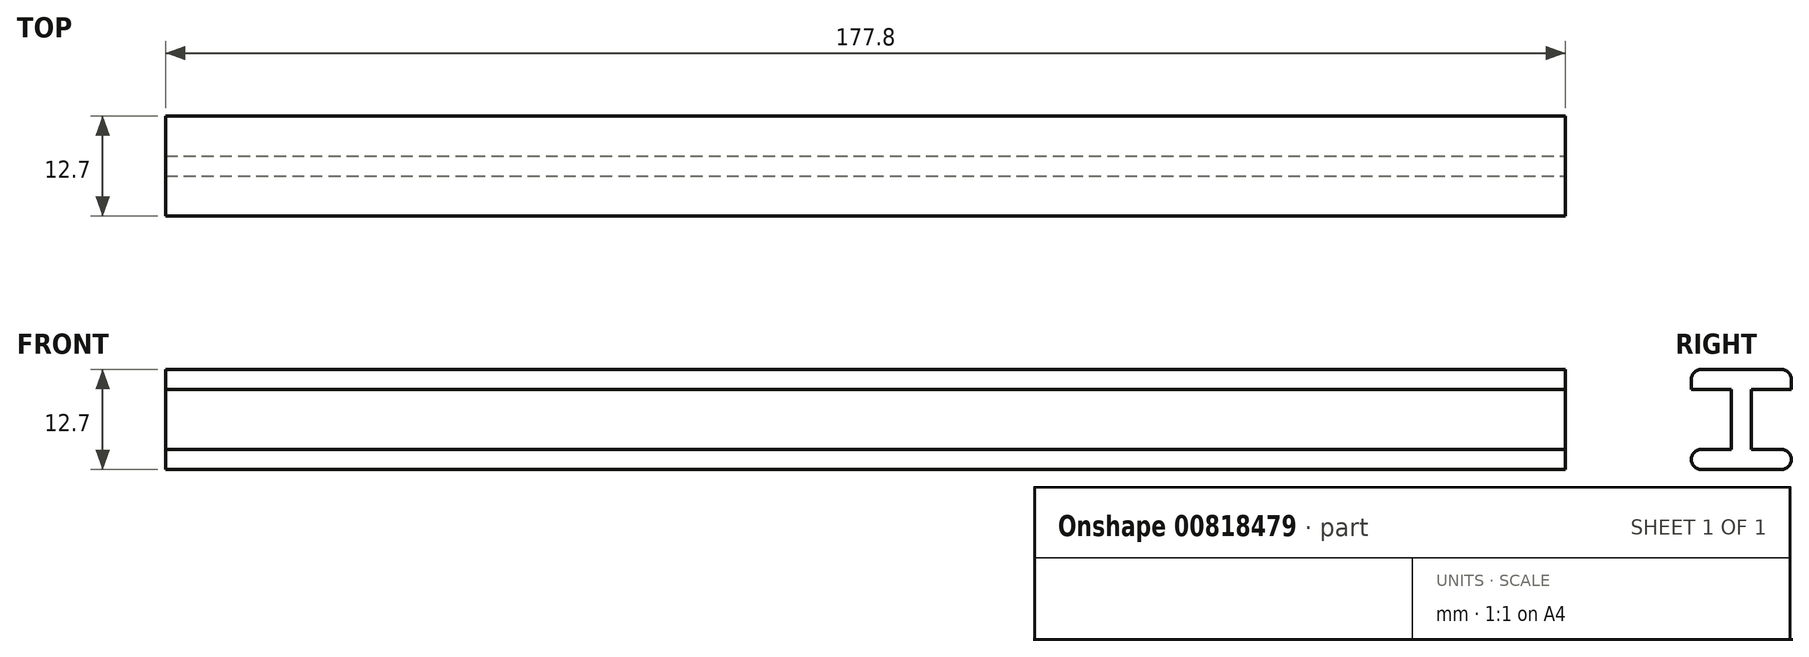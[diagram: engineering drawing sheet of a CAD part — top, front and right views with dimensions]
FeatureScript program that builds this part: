
annotation { "Feature Type Name" : "Feature", "Feature Type Description" : "" }
export const myFeature = defineFeature(function(context is Context, id is Id, definition is map)
    precondition{}
    {
        {
            var Q0;
            Q0=qCreatedBy(makeId("Top.planeOp"),FACE);
            var sketch = newSketch(context, id + "F0", { "sketchPlane" : qUnion([Q0])});
            skLineSegment(sketch, "E0.bottom", {"start": v(-88.9, 6.35) * mm, "end": v(88.9, 6.35) * mm});
            skLineSegment(sketch, "E0.top", {"start": v(-88.9, -6.35) * mm, "end": v(88.9, -6.35) * mm});
            skLineSegment(sketch, "E0.left", {"start": v(-88.9, 6.35) * mm, "end": v(-88.9, -6.35) * mm});
            skLineSegment(sketch, "E0.right", {"start": v(88.9, 6.35) * mm, "end": v(88.9, -6.35) * mm});
            skPoint(sketch, "E0.middle", {"position": v(0, 0) * mm});
            skSolve(sketch);
        }
        {
            var Q0;
            Q0=makeQuery(id+"F0.imprint","IMPRINT",FACE,{"disambiguationData":[TD([[makeQuery(id+"F0.imprint","IMPRINT",EDGE,{"derivedFrom":sQuery(id+"F0.wireOp",EDGE,"E0.bottom")}),-1.0]])]});
            extrude(context, id + "F1", {"entities" : qUnion([Q0]), "depth" : 12.7 * mm, "offsetDistance" : 25.4 * mm});
        }
        {
            var Q0;
            Q0=makeQuery(id+"F1.opExtrude","CAP_EDGE",EDGE,{"disambiguationData":[OSD([sQuery(id+"F0.wireOp",EDGE,"E0.bottom")])],"isStart":true});
            var Q1;
            Q1=makeQuery(id+"F1.opExtrude","CAP_EDGE",EDGE,{"disambiguationData":[OSD([sQuery(id+"F0.wireOp",EDGE,"E0.top")])],"isStart":false});
            var Q2;
            Q2=makeQuery(id+"F1.opExtrude","CAP_EDGE",EDGE,{"disambiguationData":[OSD([sQuery(id+"F0.wireOp",EDGE,"E0.top")])],"isStart":true});
            var Q3;
            Q3=makeQuery(id+"F1.opExtrude","CAP_EDGE",EDGE,{"disambiguationData":[OSD([sQuery(id+"F0.wireOp",EDGE,"E0.bottom")])],"isStart":false});
            fillet(context, id + "F2", {"entities" : qUnion([Q0, Q1, Q2, Q3]), "radius" : 1.27 * mm, "tangentPropagation" : true, "allowEdgeOverflow" : false});
        }
        {
            var Q0;
            Q0=makeQuery(id+"F1.opExtrude","SWEPT_FACE",FACE,{"disambiguationData":[OSD([sQuery(id+"F0.wireOp",EDGE,"E0.right")])]});
            var sketch = newSketch(context, id + "F3", { "sketchPlane" : qUnion([Q0])});
            skLineSegment(sketch, "E1.bottom", {"start": v(-6.35, 10.16) * mm, "end": v(-1.27, 10.16) * mm});
            skLineSegment(sketch, "E1.top", {"start": v(-6.35, 2.54) * mm, "end": v(-1.27, 2.54) * mm});
            skLineSegment(sketch, "E1.left", {"start": v(-6.35, 10.16) * mm, "end": v(-6.35, 2.54) * mm});
            skLineSegment(sketch, "E1.right", {"start": v(-1.27, 10.16) * mm, "end": v(-1.27, 2.54) * mm});
            skLineSegment(sketch, "E2.bottom", {"start": v(6.35, 10.16) * mm, "end": v(1.27, 10.16) * mm});
            skLineSegment(sketch, "E2.top", {"start": v(6.35, 2.54) * mm, "end": v(1.27, 2.54) * mm});
            skLineSegment(sketch, "E2.left", {"start": v(6.35, 10.16) * mm, "end": v(6.35, 2.54) * mm});
            skLineSegment(sketch, "E2.right", {"start": v(1.27, 10.16) * mm, "end": v(1.27, 2.54) * mm});
            skSolve(sketch);
        }
        {
            var Q0;
            Q0=makeQuery(id+"F3.imprint","IMPRINT",FACE,{"disambiguationData":[TD([[makeQuery(id+"F3.imprint","IMPRINT",EDGE,{"derivedFrom":sQuery(id+"F3.wireOp",EDGE,"E1.bottom")}),-1.0]])]});
            var Q1;
            Q1=makeQuery(id+"F3.imprint","IMPRINT",FACE,{"disambiguationData":[TD([[makeQuery(id+"F3.imprint","IMPRINT",EDGE,{"derivedFrom":sQuery(id+"F3.wireOp",EDGE,"E2.bottom")}),1.0]])]});
            extrude(context, id + "F4", {"entities" : qUnion([Q0, Q1]), "operationType" : NewBodyOperationType.REMOVE, "oppositeDirection" : true, "depth" : 177.8 * mm, "offsetDistance" : 25.4 * mm});
        }
        {
            var Q0;
            Q0=makeQuery(id+"F4.boolean.opBoolean","COPY",EDGE,{"derivedFrom":makeQuery(id+"F4.opExtrude","SWEPT_EDGE",EDGE,{"disambiguationData":[OSD([sQuery(id+"F0.wireOp",EDGE,"E0.top"),sQuery(id+"F0.wireOp",EDGE,"E0.right"),sQuery(id+"F3.wireOp",EDGE,"E1.bottom"),sQuery(id+"F3.wireOp",EDGE,"E1.left")])]})});
            var Q1;
            Q1=makeQuery(id+"F4.boolean.opBoolean","COPY",EDGE,{"derivedFrom":makeQuery(id+"F4.opExtrude","SWEPT_EDGE",EDGE,{"disambiguationData":[OSD([sQuery(id+"F0.wireOp",EDGE,"E0.top"),sQuery(id+"F0.wireOp",EDGE,"E0.right"),sQuery(id+"F3.wireOp",EDGE,"E1.top"),sQuery(id+"F3.wireOp",EDGE,"E1.left")])]})});
            var Q2;
            Q2=makeQuery(id+"F4.boolean.opBoolean","COPY",EDGE,{"derivedFrom":makeQuery(id+"F4.opExtrude","SWEPT_EDGE",EDGE,{"disambiguationData":[OSD([sQuery(id+"F0.wireOp",EDGE,"E0.bottom"),sQuery(id+"F0.wireOp",EDGE,"E0.right"),sQuery(id+"F3.wireOp",EDGE,"E2.bottom"),sQuery(id+"F3.wireOp",EDGE,"E2.left")])]})});
            var Q3;
            Q3=makeQuery(id+"F4.boolean.opBoolean","COPY",EDGE,{"derivedFrom":makeQuery(id+"F4.opExtrude","SWEPT_EDGE",EDGE,{"disambiguationData":[OSD([sQuery(id+"F0.wireOp",EDGE,"E0.bottom"),sQuery(id+"F0.wireOp",EDGE,"E0.right"),sQuery(id+"F3.wireOp",EDGE,"E2.top"),sQuery(id+"F3.wireOp",EDGE,"E2.left")])]})});
            fillet(context, id + "F5", {"entities" : qUnion([Q0, Q1, Q2, Q3]), "radius" : 1.27 * mm, "tangentPropagation" : true, "allowEdgeOverflow" : false});
        }
    });
